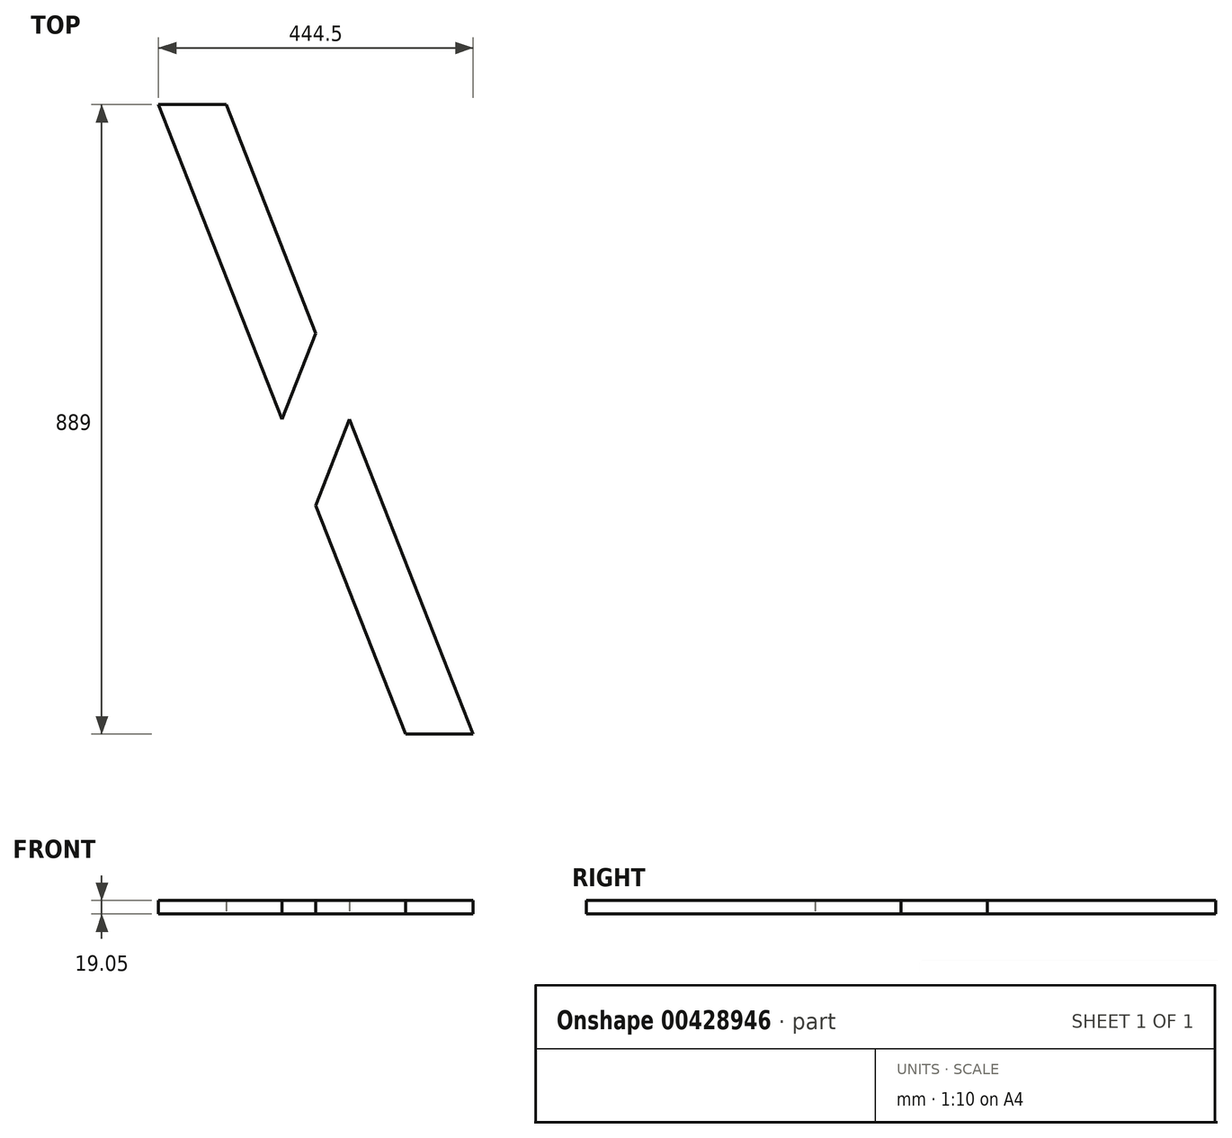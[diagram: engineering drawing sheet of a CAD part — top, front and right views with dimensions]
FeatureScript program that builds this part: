
annotation { "Feature Type Name" : "Feature", "Feature Type Description" : "" }
export const myFeature = defineFeature(function(context is Context, id is Id, definition is map)
    precondition{}
    {
        {
            var Q0;
            Q0=qCreatedBy(makeId("Top.planeOp"),FACE);
            var sketch = newSketch(context, id + "F0", { "sketchPlane" : qUnion([Q0])});
            skLineSegment(sketch, "E0.bottom", {"start": v(-343.21, 779.55) * mm, "end": v(101.29, 779.55) * mm, "construction": true});
            skLineSegment(sketch, "E0.top", {"start": v(-343.21, -109.45) * mm, "end": v(101.29, -109.45) * mm, "construction": true});
            skLineSegment(sketch, "E0.left", {"start": v(-343.21, 779.55) * mm, "end": v(-343.21, -109.45) * mm, "construction": true});
            skLineSegment(sketch, "E0.right", {"start": v(101.29, 779.55) * mm, "end": v(101.29, -109.45) * mm, "construction": true});
            skLineSegment(sketch, "E1", {"start": v(-343.21, 779.55) * mm, "end": v(-168.72, 335.05) * mm});
            skLineSegment(sketch, "E2", {"start": v(5.78, -109.45) * mm, "end": v(101.29, -109.45) * mm});
            skLineSegment(sketch, "E3", {"start": v(101.29, -109.45) * mm, "end": v(-73.21, 335.05) * mm});
            skLineSegment(sketch, "E4", {"start": v(-247.7, 779.55) * mm, "end": v(-343.21, 779.55) * mm});
            skLineSegment(sketch, "E5", {"start": v(-168.72, 335.05) * mm, "end": v(-120.96, 456.7) * mm});
            skLineSegment(sketch, "E6", {"start": v(5.78, 779.55) * mm, "end": v(101.29, 779.55) * mm, "construction": true});
            skLineSegment(sketch, "E7", {"start": v(-73.21, 335.05) * mm, "end": v(-120.96, 213.41) * mm});
            skLineSegment(sketch, "E8", {"start": v(-247.7, -109.45) * mm, "end": v(-343.21, -109.45) * mm, "construction": true});
            skLineSegment(sketch, "E9.trimOffspring", {"start": v(-120.96, 213.41) * mm, "end": v(5.78, -109.45) * mm});
            skLineSegment(sketch, "E10.trimOffspring", {"start": v(-120.96, 456.7) * mm, "end": v(-247.7, 779.55) * mm});
            skSolve(sketch);
        }
        {
            var Q0;
            Q0=makeQuery(id+"F0.imprint","IMPRINT",FACE,{"disambiguationData":[TD([[makeQuery(id+"F0.imprint","IMPRINT",EDGE,{"derivedFrom":sQuery(id+"F0.wireOp",EDGE,"E2")}),1.0]])]});
            var Q1;
            Q1=makeQuery(id+"F0.imprint","IMPRINT",FACE,{"disambiguationData":[TD([[makeQuery(id+"F0.imprint","IMPRINT",EDGE,{"derivedFrom":sQuery(id+"F0.wireOp",EDGE,"E1")}),1.0]])]});
            extrude(context, id + "F1", {"entities" : qUnion([Q0, Q1]), "depth" : 19.05 * mm});
        }
    });
